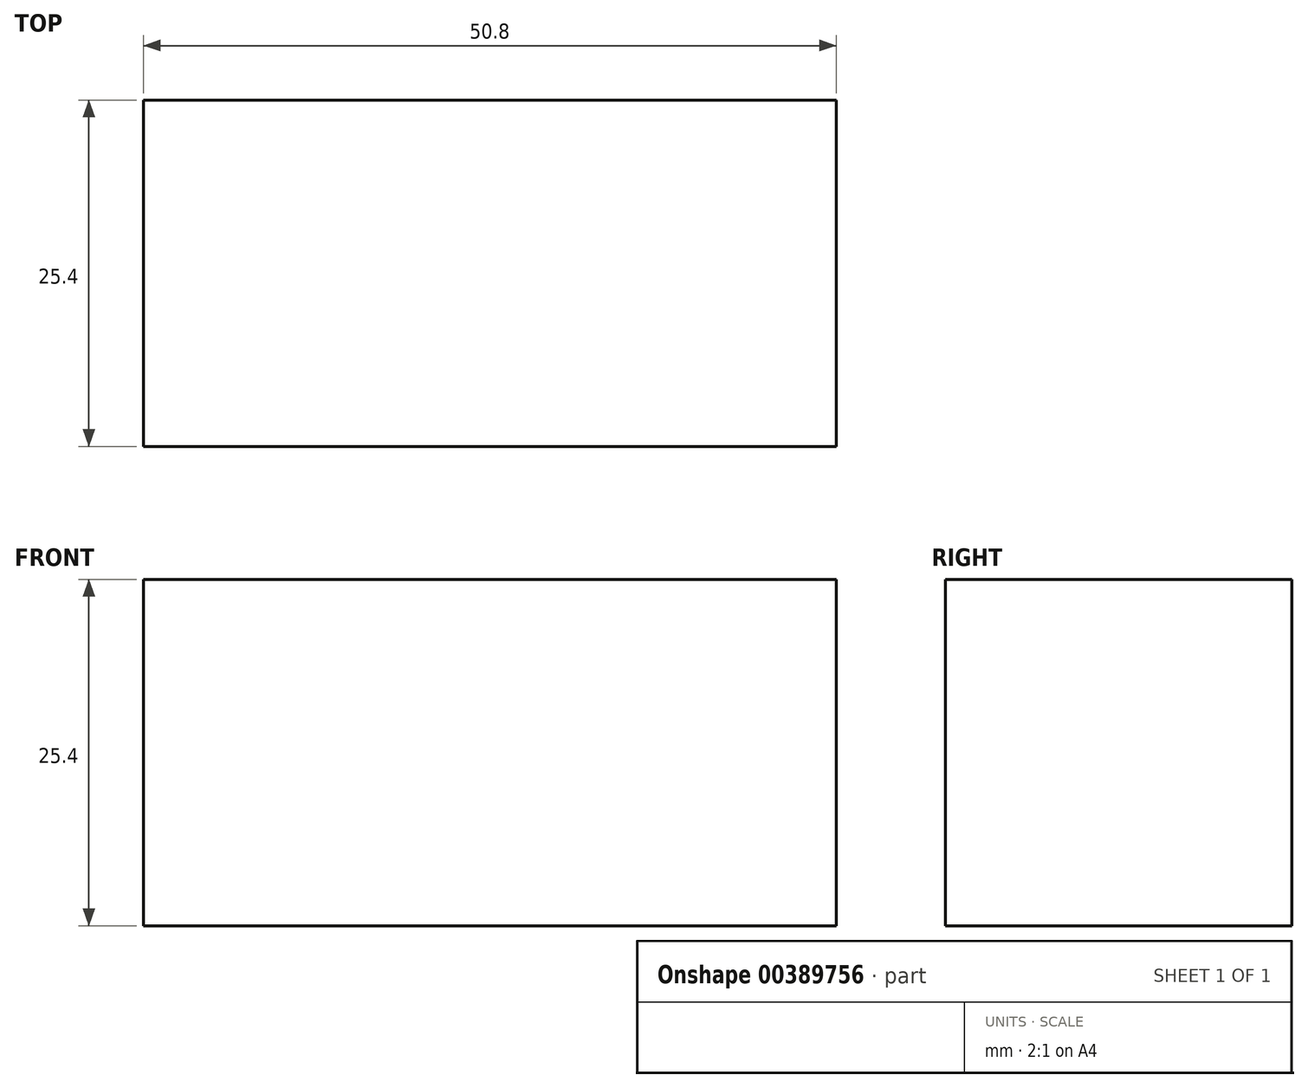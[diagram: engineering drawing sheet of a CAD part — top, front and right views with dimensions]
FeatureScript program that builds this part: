
annotation { "Feature Type Name" : "Feature", "Feature Type Description" : "" }
export const myFeature = defineFeature(function(context is Context, id is Id, definition is map)
    precondition{}
    {
        {
            var Q0;
            Q0=qCreatedBy(makeId("Front.planeOp"),FACE);
            var sketch = newSketch(context, id + "F0", { "sketchPlane" : qUnion([Q0])});
            skLineSegment(sketch, "E0.bottom", {"start": v(0, 0) * mm, "end": v(25.4, 0) * mm});
            skLineSegment(sketch, "E0.top", {"start": v(0, 25.4) * mm, "end": v(25.4, 25.4) * mm});
            skLineSegment(sketch, "E0.left", {"start": v(0, 0) * mm, "end": v(0, 25.4) * mm});
            skLineSegment(sketch, "E0.right", {"start": v(25.4, 0) * mm, "end": v(25.4, 25.4) * mm});
            skLineSegment(sketch, "E1.bottom", {"start": v(25.4, 25.4) * mm, "end": v(0, 25.4) * mm});
            skLineSegment(sketch, "E1.top", {"start": v(25.4, 50.8) * mm, "end": v(0, 50.8) * mm});
            skLineSegment(sketch, "E1.left", {"start": v(25.4, 25.4) * mm, "end": v(25.4, 50.8) * mm});
            skLineSegment(sketch, "E1.right", {"start": v(0, 25.4) * mm, "end": v(0, 50.8) * mm});
            skLineSegment(sketch, "E2.bottom", {"start": v(25.4, 25.4) * mm, "end": v(50.8, 25.4) * mm});
            skLineSegment(sketch, "E2.top", {"start": v(25.4, 0) * mm, "end": v(50.8, 0) * mm});
            skLineSegment(sketch, "E2.left", {"start": v(25.4, 25.4) * mm, "end": v(25.4, 0) * mm});
            skLineSegment(sketch, "E2.right", {"start": v(50.8, 25.4) * mm, "end": v(50.8, 0) * mm});
            skSolve(sketch);
        }
        {
            var Q0;
            Q0=makeQuery(id+"F0.imprint","IMPRINT",FACE,{"disambiguationData":[TD([[makeQuery(id+"F0.imprint","IMPRINT",EDGE,{"derivedFrom":sQuery(id+"F0.wireOp",EDGE,"E1.bottom")}),-1.0]])]});
            var Q1;
            Q1=makeQuery(id+"F0.imprint","IMPRINT",FACE,{"disambiguationData":[TD([[makeQuery(id+"F0.imprint","IMPRINT",EDGE,{"derivedFrom":sQuery(id+"F0.wireOp",EDGE,"E0.bottom")}),1.0]])]});
            var Q2;
            Q2=makeQuery(id+"F0.imprint","IMPRINT",FACE,{"disambiguationData":[TD([[makeQuery(id+"F0.imprint","IMPRINT",EDGE,{"derivedFrom":sQuery(id+"F0.wireOp",EDGE,"E2.bottom")}),-1.0]])]});
            extrude(context, id + "F1", {"entities" : qUnion([Q0, Q1, Q2]), "depth" : 25.4 * mm});
        }
    });
